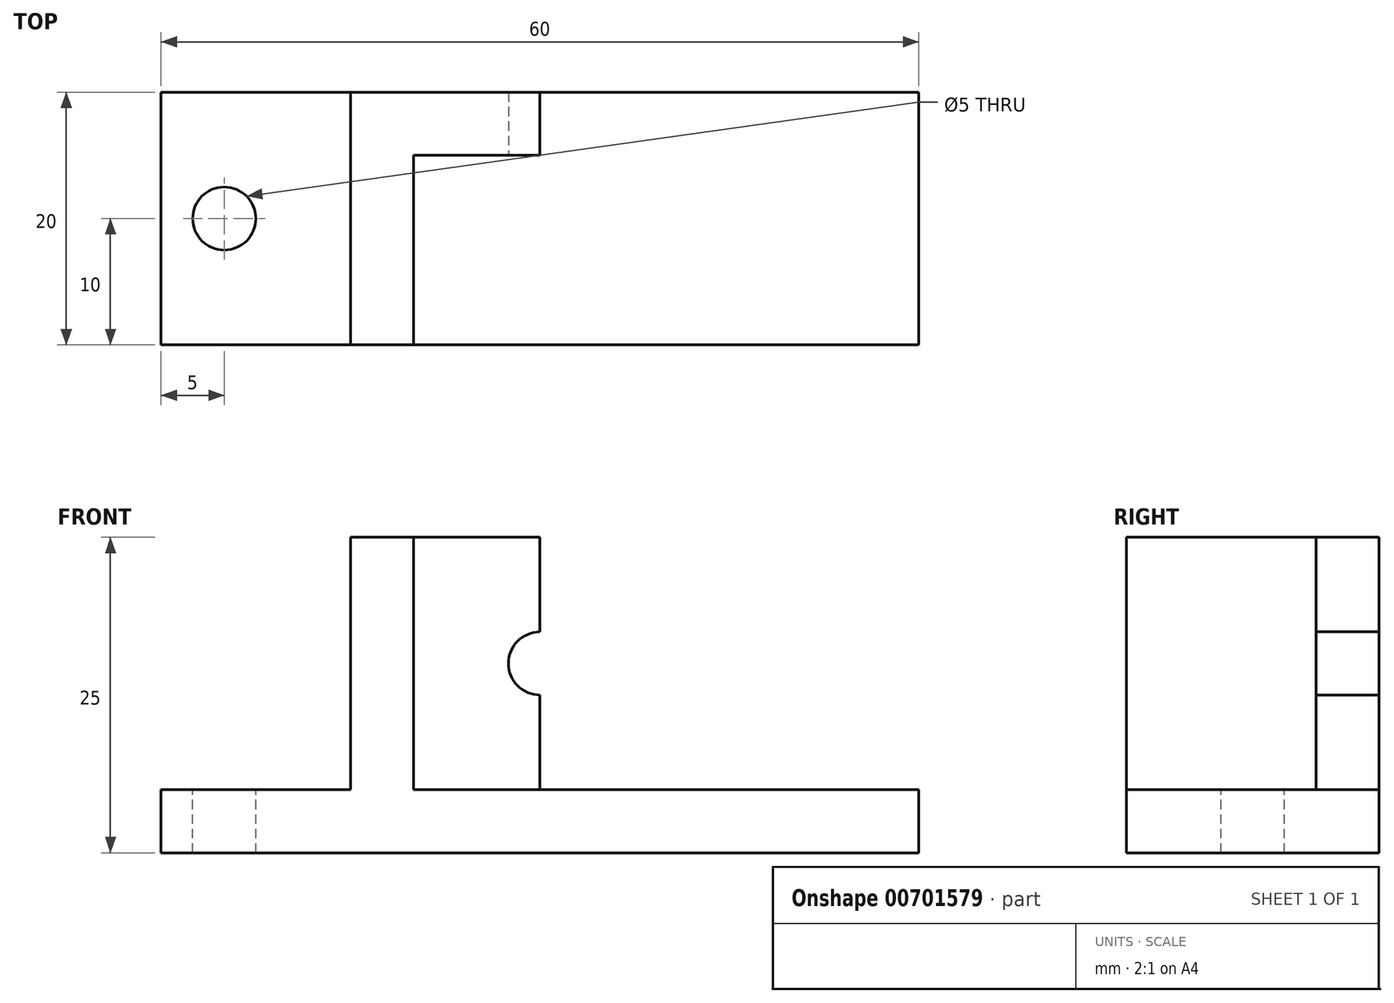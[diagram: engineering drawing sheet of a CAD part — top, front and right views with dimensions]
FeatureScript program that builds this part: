
annotation { "Feature Type Name" : "Feature", "Feature Type Description" : "" }
export const myFeature = defineFeature(function(context is Context, id is Id, definition is map)
    precondition{}
    {
        {
            var Q0;
            Q0=qCreatedBy(makeId("Top.planeOp"),FACE);
            var sketch = newSketch(context, id + "F0", { "sketchPlane" : qUnion([Q0])});
            skLineSegment(sketch, "E0.bottom", {"start": v(-30, 10) * mm, "end": v(30, 10) * mm});
            skLineSegment(sketch, "E0.top", {"start": v(-30, -10) * mm, "end": v(30, -10) * mm});
            skLineSegment(sketch, "E0.left", {"start": v(-30, 10) * mm, "end": v(-30, -10) * mm});
            skLineSegment(sketch, "E0.right", {"start": v(30, 10) * mm, "end": v(30, -10) * mm});
            skSolve(sketch);
        }
        {
            var Q0;
            Q0 = qSketchRegion(id + "F0", true);
            extrude(context, id + "F1", {"entities" : qUnion([Q0]), "depth" : 5 * mm, "offsetDistance" : 25 * mm});
        }
        {
            var Q0;
            Q0=makeQuery(id+"F1.opExtrude","CAP_FACE",FACE,{"disambiguationData":[OSD([sQuery(id+"F0.wireOp",EDGE,"E0.bottom"),sQuery(id+"F0.wireOp",EDGE,"E0.top"),sQuery(id+"F0.wireOp",EDGE,"E0.left"),sQuery(id+"F0.wireOp",EDGE,"E0.right")])],"isStart":false});
            var sketch = newSketch(context, id + "F2", { "sketchPlane" : qUnion([Q0])});
            skLineSegment(sketch, "E1.top", {"start": v(-15, -10) * mm, "end": v(-10, -10) * mm});
            skLineSegment(sketch, "E1.left", {"start": v(-15, 10) * mm, "end": v(-15, -10) * mm});
            skLineSegment(sketch, "E1.right", {"start": v(-10, 5) * mm, "end": v(-10, -10) * mm});
            skLineSegment(sketch, "E2", {"start": v(-10, 5) * mm, "end": v(0, 5) * mm});
            skLineSegment(sketch, "E3", {"start": v(0, 5) * mm, "end": v(0, 10) * mm});
            skLineSegment(sketch, "E4", {"start": v(-15, 10) * mm, "end": v(0, 10) * mm});
            skSolve(sketch);
        }
        {
            var Q0;
            Q0 = qSketchRegion(id + "F2", true);
            extrude(context, id + "F3", {"entities" : qUnion([Q0]), "operationType" : NewBodyOperationType.ADD, "depth" : 20 * mm, "offsetDistance" : 25 * mm});
        }
        {
            var Q0;
            {var subQ0=sQuery(id+"F0.wireOp",EDGE,"E0.left");var subQ1=sQuery(id+"F0.wireOp",EDGE,"E0.top");var subQ2=sQuery(id+"F0.wireOp",EDGE,"E0.bottom");Q0=makeQuery(id+"F3.boolean.opBoolean","SPLIT",FACE,{"disambiguationData":[TD([makeQuery(id+"F1.opExtrude","SWEPT_FACE",FACE,{"disambiguationData":[OSD([subQ0])]})])],"derivedFrom":makeQuery(id+"F1.opExtrude","CAP_FACE",FACE,{"disambiguationData":[OSD([subQ2,subQ1,subQ0,sQuery(id+"F0.wireOp",EDGE,"E0.right")])],"isStart":false})});}
            var sketch = newSketch(context, id + "F4", { "sketchPlane" : qUnion([Q0])});
            skCircle(sketch, "E5", {"center": v(-25, 0) * mm, "radius": 2.1 * mm});
            skSolve(sketch);
        }
        {
            var Q0;
            Q0=sQuery(id+"F4.wireOp",VERTEX,"E5.center");
            var Q1;
            Q1=makeQuery(id+"F1.opExtrude","SWEPT_BODY",BODY,{"disambiguationData":[OSD([sQuery(id+"F0.wireOp",EDGE,"E0.bottom"),sQuery(id+"F0.wireOp",EDGE,"E0.top"),sQuery(id+"F0.wireOp",EDGE,"E0.left"),sQuery(id+"F0.wireOp",EDGE,"E0.right")])]});
            hole(context, id + "F5", {"style" : HoleStyle.SIMPLE, "endStyle" : HoleEndStyle.THROUGH, "holeDiameter" : 5 * mm, "majorDiameter" : 5 * mm, "isTappedThrough" : true, "tappedDepth" : 12 * mm, "tapClearance" : 3, "locations" : qUnion([Q0]), "scope" : qUnion([Q1])});
        }
        {
            var Q0;
            {var subQ0=sQuery(id+"F2.wireOp",EDGE,"E2");Q0=makeQuery(id+"FZoU6tEqUhYTevg_1.1.F3.boolean.opBoolean","MERGE",FACE,{"derivedFrom":[makeQuery(id+"F3.opExtrude","SWEPT_FACE",FACE,{"disambiguationData":[OSD([subQ0])]}),makeQuery(id+"FZoU6tEqUhYTevg_1.1.F3.opExtrude","SWEPT_FACE",FACE,{"disambiguationData":[OSD([subQ0])]})]});}
            var sketch = newSketch(context, id + "F6", { "sketchPlane" : qUnion([Q0])});
            skCircle(sketch, "E6", {"center": v(0, 15) * mm, "radius": 2.1 * mm});
            skSolve(sketch);
        }
        {
            var Q0;
            Q0=sQuery(id+"F6.wireOp",VERTEX,"E6.center");
            var Q1;
            Q1=makeQuery(id+"F1.opExtrude","SWEPT_BODY",BODY,{"disambiguationData":[OSD([sQuery(id+"F0.wireOp",EDGE,"E0.bottom"),sQuery(id+"F0.wireOp",EDGE,"E0.top"),sQuery(id+"F0.wireOp",EDGE,"E0.left"),sQuery(id+"F0.wireOp",EDGE,"E0.right")])]});
            hole(context, id + "F7", {"style" : HoleStyle.SIMPLE, "endStyle" : HoleEndStyle.THROUGH, "holeDiameter" : 5 * mm, "majorDiameter" : 5 * mm, "isTappedThrough" : true, "tappedDepth" : 12 * mm, "tapClearance" : 3, "locations" : qUnion([Q0]), "scope" : qUnion([Q1])});
        }
    });
